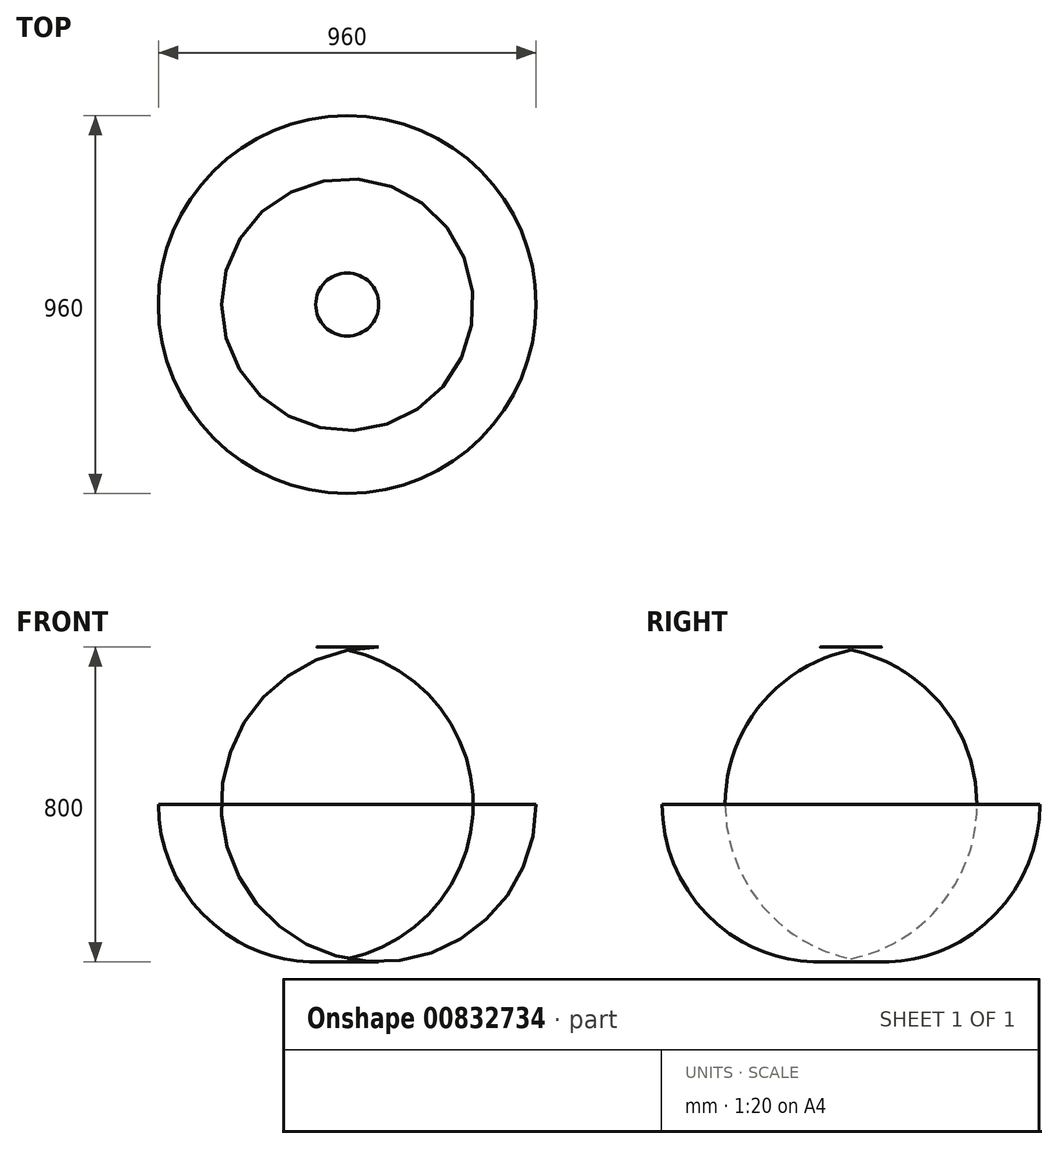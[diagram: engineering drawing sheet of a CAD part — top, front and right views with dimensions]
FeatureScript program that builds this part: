
annotation { "Feature Type Name" : "Feature", "Feature Type Description" : "" }
export const myFeature = defineFeature(function(context is Context, id is Id, definition is map)
    precondition{}
    {
        {
            var Q0;
            Q0=qCreatedBy(makeId("Top.planeOp"),FACE);
            cPlane(context, id + "F0", {"entities" : qUnion([Q0]), "cplaneType" : CPlaneType.OFFSET, "offset" : 400 * mm, "width" : 150 * mm, "height" : 150 * mm});
        }
        {
            var Q0;
            Q0=qCreatedBy(id+"F0.planeOp",FACE);
            var sketch = newSketch(context, id + "F1", { "sketchPlane" : qUnion([Q0])});
            skCircle(sketch, "E0", {"center": v(0, 0) * mm, "radius": 80 * mm});
            skSolve(sketch);
        }
        {
            var Q0;
            Q0=qCreatedBy(makeId("Front.planeOp"),FACE);
            var sketch = newSketch(context, id + "F2", { "sketchPlane" : qUnion([Q0])});
            skArc(sketch, "E1", {"start": v(-80, 400) * mm, "mid": v(-362.84, 282.84) * mm, "end": v(-480, 0) * mm});
            skArc(sketch, "E2.1.0", {"start": v(-306.41, -269.28) * mm, "mid": v(-63.53, -455.65) * mm, "end": v(240, -415.7) * mm});
            skArc(sketch, "E2.2.0", {"start": v(386.41, -130.72) * mm, "mid": v(426.37, 172.8) * mm, "end": v(240, 415.7) * mm});
            skPoint(sketch, "E2.center", {"position": v(0, 0) * mm});
            skSolve(sketch);
        }
        {
            var Q0;
            Q0=sQuery(id+"F2.wireOp",EDGE,"E1");
            var Q1;
            Q1=sQuery(id+"F1.wireOp",EDGE,"E0");
            revolve(context, id + "F3", {"bodyType" : ToolBodyType.SURFACE, "surfaceOperationType" : NewSurfaceOperationType.NEW, "surfaceEntities" : qUnion([Q0]), "axis" : qUnion([Q1]), "revolveType" : RevolveType.FULL});
        }
    });
